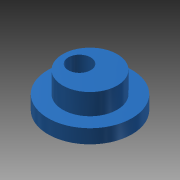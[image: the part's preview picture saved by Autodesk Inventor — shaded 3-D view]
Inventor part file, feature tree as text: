
AUTODESK INVENTOR PART (.ipt)
format: ipt  version: 2013 (Build 170138000, 138)  size: 88,576 bytes
history: native  units: mm
features: extrude x2
ambient origin geometry x8: Origin, YZ Plane, XZ Plane, XY Plane, X Axis, Y Axis, Z Axis, Center Point
bodies: Solid1 (feature_tree)
feature tree (2):
  extrude  "Extrusion1"  Depth=12.0mm
  extrude  "Extrusion2"  Depth=2.0mm TaperAngle=0.0deg
